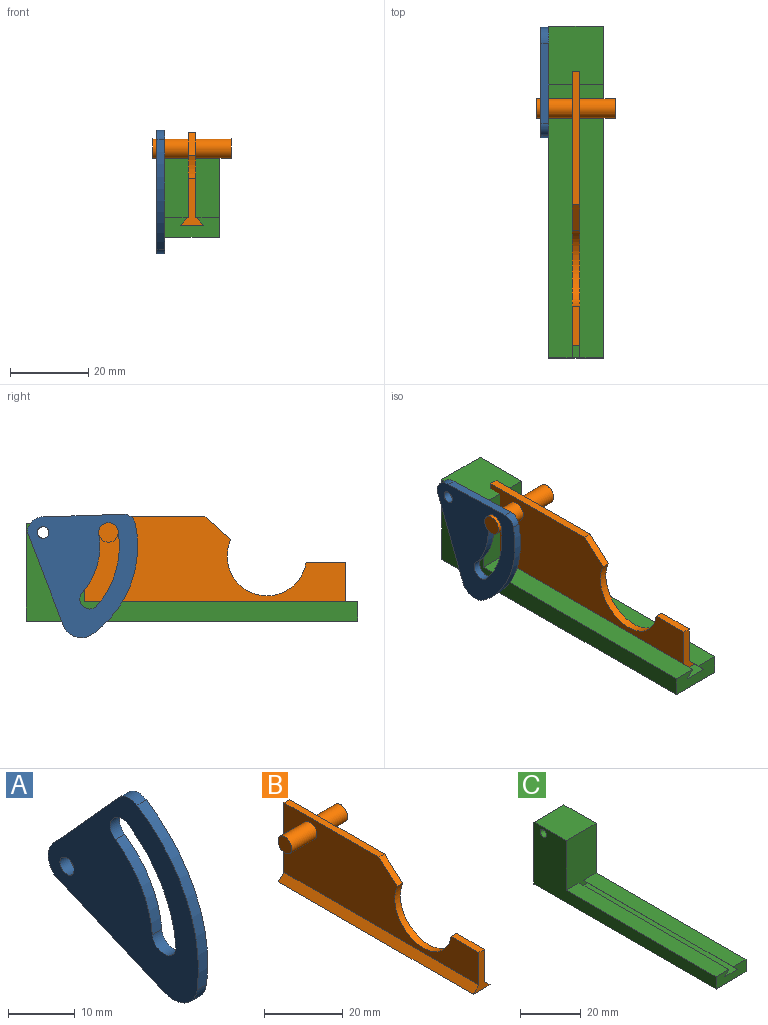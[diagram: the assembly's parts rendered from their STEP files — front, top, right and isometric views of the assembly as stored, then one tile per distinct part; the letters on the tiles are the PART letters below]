
ASSEMBLY  parts=3 mates=4
PART A: 13 faces, bbox 2x31.8x32.2 mm
  f0: cylinder r=23.12mm len=17.24mm, axis (-1,0,0), area 41.2mm2, adj f1,f10,f11,f12
  f1: cylinder r=2.5mm len=4.56mm, axis (-1,0,0), area 15.7mm2, adj f0,f2,f11,f12
  f2: cylinder r=18.12mm len=13.51mm, axis (-1,0,0), area 32.3mm2, adj f1,f10,f11,f12
  f3: cylinder r=4mm len=5.76mm, axis (-1,0,0), area 12.8mm2, adj f4,f8,f11,f12
  f4: plane 15.16x13.74mm, normal (0,0.74,0.67), area 40.9mm2, adj f3,f5,f11,f12
  f5: cylinder r=3mm len=3.82mm, axis (-1,0,0), area 8.4mm2, adj f4,f6,f11,f12
  f6: cylinder r=27.82mm len=27.48mm, axis (-1,0,0), area 64.1mm2, adj f5,f7,f11,f12
  f7: cylinder r=5mm len=6.9mm, axis (-1,0,0), area 18.3mm2, adj f6,f8,f11,f12
  f8: plane 23.41x9.94mm, normal (0,0.39,-0.92), area 50.9mm2, adj f3,f7,f11,f12
  f9: cylinder r=1.5mm len=3mm, axis (-1,0,0), area 18.8mm2, adj f11,f12
  f10: cylinder r=2.5mm len=4.99mm, axis (-1,0,0), area 15.7mm2, adj f0,f2,f11,f12
  f11: plane 32.23x31.82mm, normal (1,0,0), area 524.9mm2, adj f0,f1,f2,f3,f4,f5,f6,f7
  f12: plane 32.23x31.82mm, normal (-1,0,0), area 524.9mm2, adj f0,f1,f2,f3,f4,f5,f6,f7
PART B: 15 faces, bbox 20x70x23.7 mm
  f0: plane 70x21.75mm, normal (-1,0,0), area 1003mm2, adj f2,f3,f4,f6,f7,f8,f10,f14
  f1: plane 70x21.75mm, normal (1,0,0), area 1003mm2, adj f2,f3,f4,f6,f7,f8,f11,f13
  f2: cylinder r=10.18mm len=20.23mm, axis (-1,0,0), area 69.5mm2, adj f0,f1,f3,f8
  f3: plane 10x2mm, normal (0,0,1), area 20mm2, adj f0,f1,f2,f4
  f4: plane 12x6mm, normal (0,-1,0), area 28mm2, adj f0,f1,f3,f5,f13,f14
  f5: plane 70x6mm, normal (0,0,-1), area 420mm2, adj f4,f6,f13,f14
  f6: plane 23.6x6mm, normal (0,1,0), area 51.2mm2, adj f0,f1,f5,f7,f13,f14
  f7: plane 34.1x2mm, normal (0,0,1), area 68.2mm2, adj f0,f1,f6,f8
  f8: plane 6.61x5.85mm, normal (0,-0.66,0.75), area 17.7mm2, adj f0,f1,f2,f7
  f9: plane 5x5mm, normal (-1,0,0), area 19.6mm2, adj f10
  f10: cylinder r=2.5mm len=9mm, axis (-1,0,0), area 141.4mm2, adj f0,f9
  f11: cylinder r=2.5mm len=9mm, axis (-1,0,0), area 141.4mm2, adj f1,f12
  f12: plane 5x5mm, normal (1,0,0), area 19.6mm2, adj f11
  f13: plane 70x2mm, normal (0.71,0,0.71), area 198mm2, adj f1,f4,f5,f6
  f14: plane 70x2mm, normal (-0.71,0,0.71), area 198mm2, adj f0,f4,f5,f6
PART C: 13 faces, bbox 14x85x25 mm
  f0: plane 70x2mm, normal (-0.71,0,-0.71), area 198mm2, adj f1,f7,f8,f9
  f1: plane 70x6mm, normal (0,0,1), area 420mm2, adj f0,f2,f8,f9
  f2: plane 85x25mm, normal (1,0,0), area 717.9mm2, adj f1,f3,f8,f9,f10,f11,f12
  f3: plane 85x14mm, normal (0,0,-1), area 1190mm2, adj f2,f4,f8,f10
  f4: plane 85x25mm, normal (-1,0,0), area 717.9mm2, adj f3,f5,f8,f9,f10,f11,f12
  f5: plane 70x6mm, normal (0,0,1), area 420mm2, adj f4,f6,f8,f9
  f6: plane 70x2mm, normal (0.71,0,-0.71), area 198mm2, adj f5,f7,f8,f9
  f7: plane 70x6mm, normal (0,0,1), area 420mm2, adj f0,f6,f8,f9
  f8: plane 14x5mm, normal (0,-1,0), area 62mm2, adj f0,f1,f2,f3,f4,f5,f6,f7
  f9: plane 22x14mm, normal (0,-1,0), area 288mm2, adj f0,f1,f2,f4,f5,f6,f7,f11
  f10: plane 25x14mm, normal (0,1,0), area 350mm2, adj f2,f3,f4,f11
  f11: plane 15x14mm, normal (0,0,1), area 210mm2, adj f2,f4,f9,f10
  f12: cylinder r=1.5mm len=14mm, axis (1,0,0), area 131.9mm2, adj f2,f4
PLACE A rot(axis=(1,0,0),45.9deg) t=(-36.95,-7.42,-25.31)mm
PLACE B t=(-20.95,-26.93,16.37)mm
PLACE C t=(-20.95,-30.21,16.37)mm fixed
MATE planar A.f3 <-> C.f12  axis (1,0,0) through (-27.95,30.38,22.42)mm
MATE cylindrical C.f12 <-> A.f3  axis (1,0,0) through (-27.95,30.38,22.42)mm
MATE slider B.f4 <-> C.f8  axis (0,-1,0) through (-20.95,-46.98,2.74)mm
MATE planar C.f7 <-> B.f5  axis (0,0,1) through (-20.95,-15.25,2.74)mm
